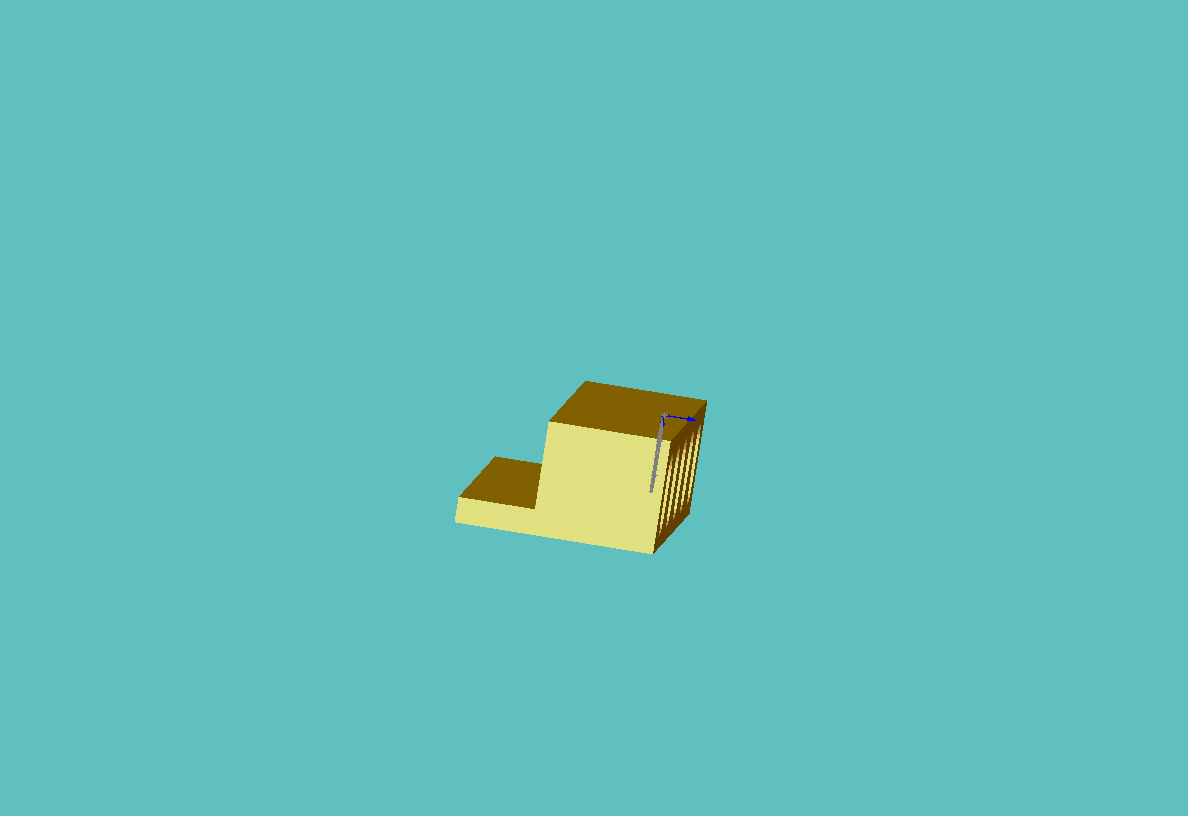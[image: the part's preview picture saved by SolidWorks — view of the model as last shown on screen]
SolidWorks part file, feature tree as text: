
SOLIDWORKS PART (.sldprt)
format: sldprt  version: not decoded by parser v0  size: 444,416 bytes
history: native  units: mm
features: sketch x4, extrude x2, cut_extrude x2, material x1, pattern_linear x1, fillet x1, boolean_combine x1 (+10 scaffold rows collapsed)
feature tree (22):
  scaffold x10  (default folders/planes/origin — collapsed)
  material  "Material <not specified>"
  sketch  "Sketch2"  dims[c1.D1=0.63mm c1.D2=1.0mm c1.D6=~1.190625mm c1.D3=1.25mm c1.D4=1.25mm c1.D5=2.0mm c2.D6=3.1mm c2.D7=1.75mm c2.D8=1.25mm c3.D6=1.5mm c3.D7=~2.402992mm c3.D3=0.7mm]
  sketch  "Sketch3"  dims[c1.D1=1.0125mm c1.D2=~1.295313mm c1.D3=~1.295313mm c2.D1=2.2mm c2.D2=2.5mm c2.D3=~1.726997mm c3.D3=~9.117994deg c4.D3=3.0mm c4.D4=2.2mm c4.D5=1.8875mm c4.D1=2.2mm c4.D2=2.5mm c5.D3=3.5mm]
  extrude  "Extrude1"  Depth=2.2mm
  sketch  "Sketch4"  dims[c1.D2=0.7mm c1.D1=0.7mm c2.D2=0.7mm]
  cut_extrude  "top piece well"  [1 undecoded]
  cut_extrude  "0-80 and 23Ga holes"  [1 undecoded]
  pattern_linear  "mold linear pattern"  Count1=5 Count2=1 Spacing1=6mm Spacing2=50mm
  fillet  "mold fillet"  Radius=0.5mm
  sketch  "Sketch5"  dims[D1=1.5mm]
  extrude  "23Ga set ledge"  Depth=9.5mm
  boolean_combine  "Combine1"
decode coverage: 8 of 11 modeling features carry decoded parameters
note: ~ marks probable driven/reference dimensions
note: 2 parameter values undecoded
note: suppression state not decoded; provenance and decode notes live in map.json
